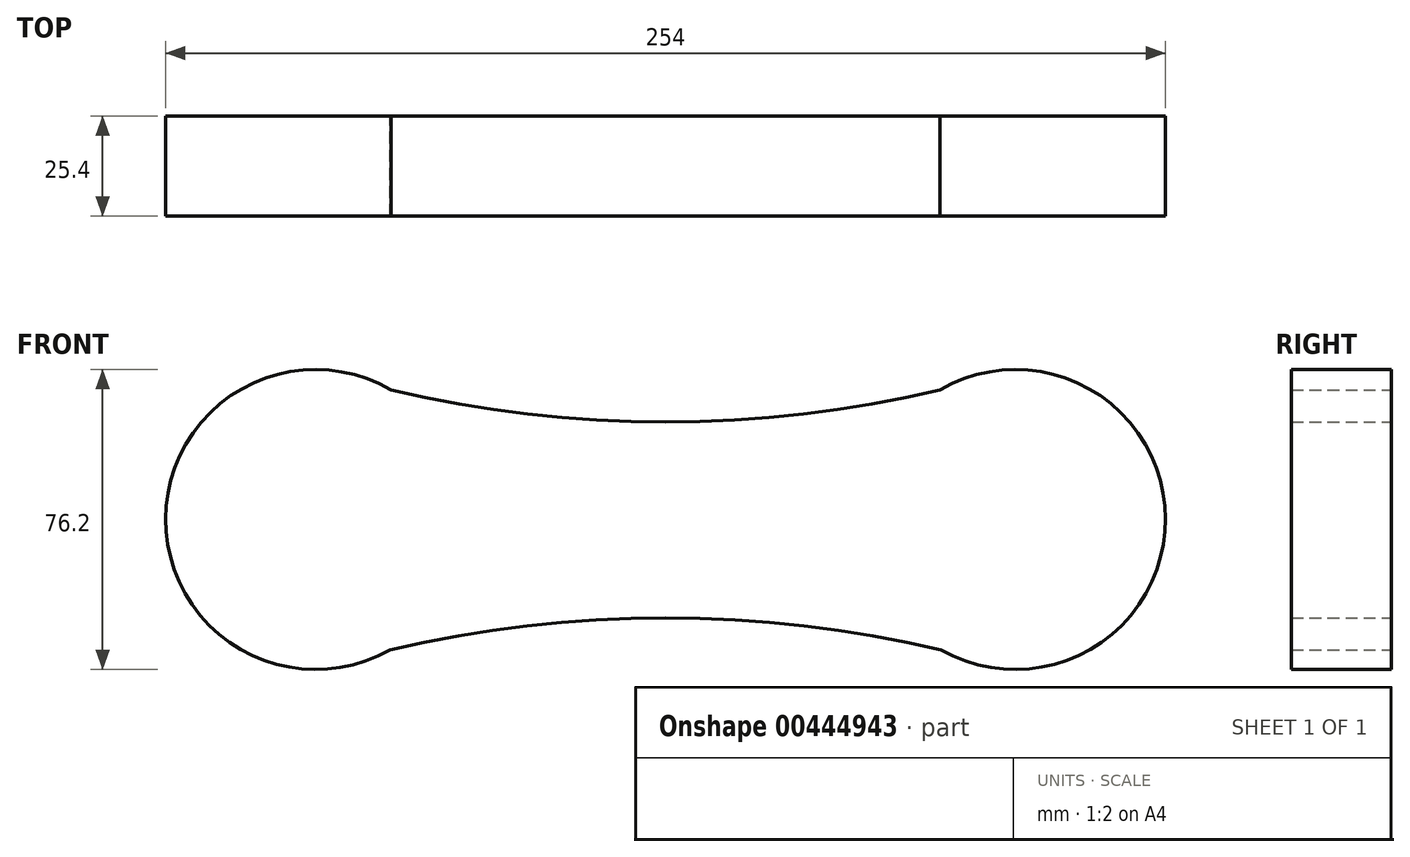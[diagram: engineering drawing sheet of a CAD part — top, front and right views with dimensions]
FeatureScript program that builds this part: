
annotation { "Feature Type Name" : "Feature", "Feature Type Description" : "" }
export const myFeature = defineFeature(function(context is Context, id is Id, definition is map)
    precondition{}
    {
        {
            var Q0;
            Q0=qCreatedBy(makeId("Front.planeOp"),FACE);
            var sketch = newSketch(context, id + "F0", { "sketchPlane" : qUnion([Q0])});
            skCircle(sketch, "E0", {"center": v(-87.94, 0.75) * mm, "radius": 38.1 * mm});
            skCircle(sketch, "E1", {"center": v(89.86, 0.75) * mm, "radius": 38.1 * mm});
            skArc(sketch, "E2", {"start": v(-87.94, 38.85) * mm, "mid": v(0.96, 25.53) * mm, "end": v(89.86, 38.85) * mm});
            skArc(sketch, "E3", {"start": v(89.86, -37.35) * mm, "mid": v(0.96, -24.31) * mm, "end": v(-87.94, -37.35) * mm});
            skSolve(sketch);
        }
        {
            var Q0;
            Q0 = qSketchRegion(id + "F0", true);
            extrude(context, id + "F1", {"entities" : qUnion([Q0]), "depth" : 25.4 * mm});
        }
    });
